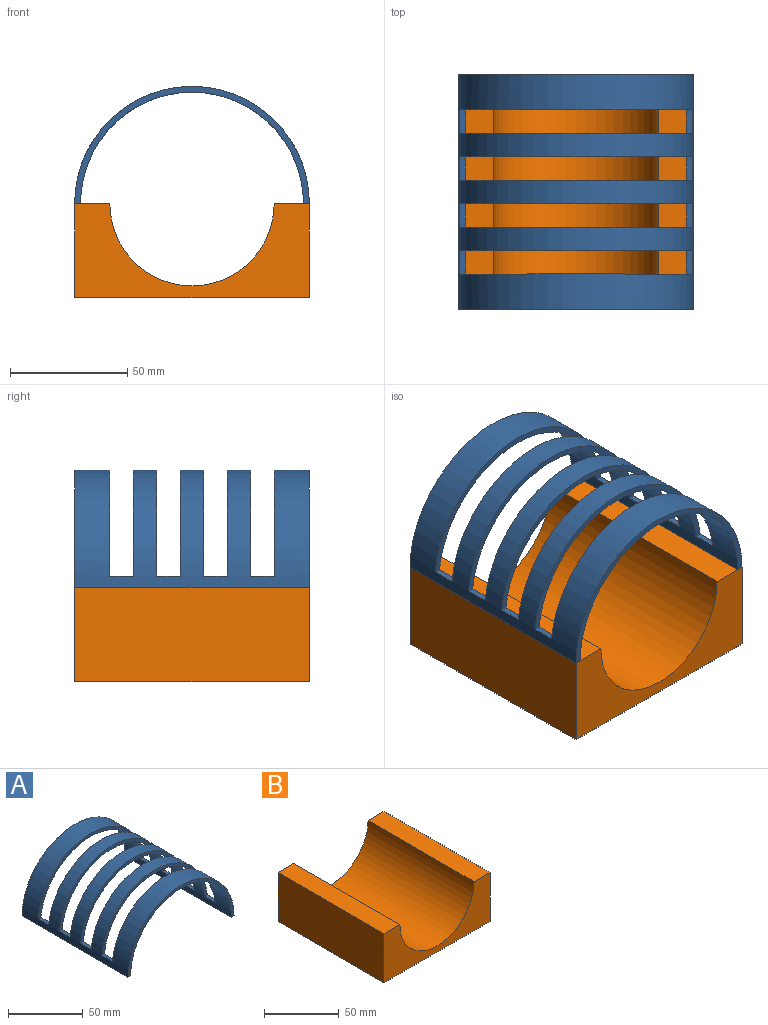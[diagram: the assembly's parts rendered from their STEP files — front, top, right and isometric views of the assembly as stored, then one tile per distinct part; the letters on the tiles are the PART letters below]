
ASSEMBLY  parts=2 mates=1
PART A: 22 faces, bbox 100x100x50 mm
  f0: plane 100x2.5mm, normal (0,0,-1), area 250mm2, adj f1,f3,f4,f5
  f1: cylinder r=50mm len=100mm, axis (0,1,0), area 9825.4mm2, adj f0,f2,f4,f5,f6,f7,f8,f9
  f2: plane 100x2.5mm, normal (0,0,-1), area 250mm2, adj f1,f3,f4,f5
  f3: cylinder r=47.5mm len=100mm, axis (0,1,0), area 9354.3mm2, adj f0,f2,f4,f5,f6,f7,f8,f9
  f4: plane 100x50mm, normal (0,-1,0), area 382.9mm2, adj f0,f1,f2,f3
  f5: plane 100x50mm, normal (0,1,0), area 382.9mm2, adj f0,f1,f2,f3
  f6: plane 99.5x45mm, normal (0,1,0), area 357.8mm2, adj f1,f3,f7,f8
  f7: plane 10x2.51mm, normal (0,0,1), area 25.1mm2, adj f1,f3,f6,f9
  f8: plane 10x2.51mm, normal (0,0,1), area 25.1mm2, adj f1,f3,f6,f9
  f9: plane 99.5x45mm, normal (0,-1,0), area 357.8mm2, adj f1,f3,f7,f8
  f10: plane 99.5x45mm, normal (0,1,0), area 357.8mm2, adj f1,f3,f11,f12
  f11: plane 10x2.51mm, normal (0,0,1), area 25.1mm2, adj f1,f3,f10,f13
  f12: plane 10x2.51mm, normal (0,0,1), area 25.1mm2, adj f1,f3,f10,f13
  f13: plane 99.5x45mm, normal (0,-1,0), area 357.8mm2, adj f1,f3,f11,f12
  f14: plane 99.5x45mm, normal (0,1,0), area 357.8mm2, adj f1,f3,f15,f16
  f15: plane 10x2.51mm, normal (0,0,1), area 25.1mm2, adj f1,f3,f14,f17
  f16: plane 10x2.51mm, normal (0,0,1), area 25.1mm2, adj f1,f3,f14,f17
  f17: plane 99.5x45mm, normal (0,-1,0), area 357.8mm2, adj f1,f3,f15,f16
  f18: plane 99.5x45mm, normal (0,-1,0), area 357.8mm2, adj f1,f3,f20,f21
  f19: plane 99.5x45mm, normal (0,1,0), area 357.8mm2, adj f1,f3,f20,f21
  f20: plane 10x2.51mm, normal (0,0,1), area 25.1mm2, adj f1,f3,f18,f19
  f21: plane 10x2.51mm, normal (0,0,1), area 25.1mm2, adj f1,f3,f18,f19
PART B: 8 faces, bbox 100x100x40 mm
  f0: plane 100x15mm, normal (0,0,1), area 1500mm2, adj f1,f5,f6,f7
  f1: plane 100x40mm, normal (-1,0,0), area 4000mm2, adj f0,f2,f6,f7
  f2: plane 100x100mm, normal (0,0,-1), area 10000mm2, adj f1,f3,f6,f7
  f3: plane 100x40mm, normal (1,0,0), area 4000mm2, adj f2,f4,f6,f7
  f4: plane 100x15mm, normal (0,0,1), area 1500mm2, adj f3,f5,f6,f7
  f5: cylinder r=35mm len=100mm, axis (0,1,0), area 10995.6mm2, adj f0,f4,f6,f7
  f6: plane 100x40mm, normal (0,-1,0), area 2075.8mm2, adj f0,f1,f2,f3,f4,f5
  f7: plane 100x40mm, normal (0,1,0), area 2075.8mm2, adj f0,f1,f2,f3,f4,f5
PLACE A t=(-85.86,36.98,47.46)mm
PLACE B t=(-85.86,36.98,7.46)mm
MATE fastened A.f0 <-> B.f4  axis (0,0,-1) through (-35.86,36.98,47.46)mm
